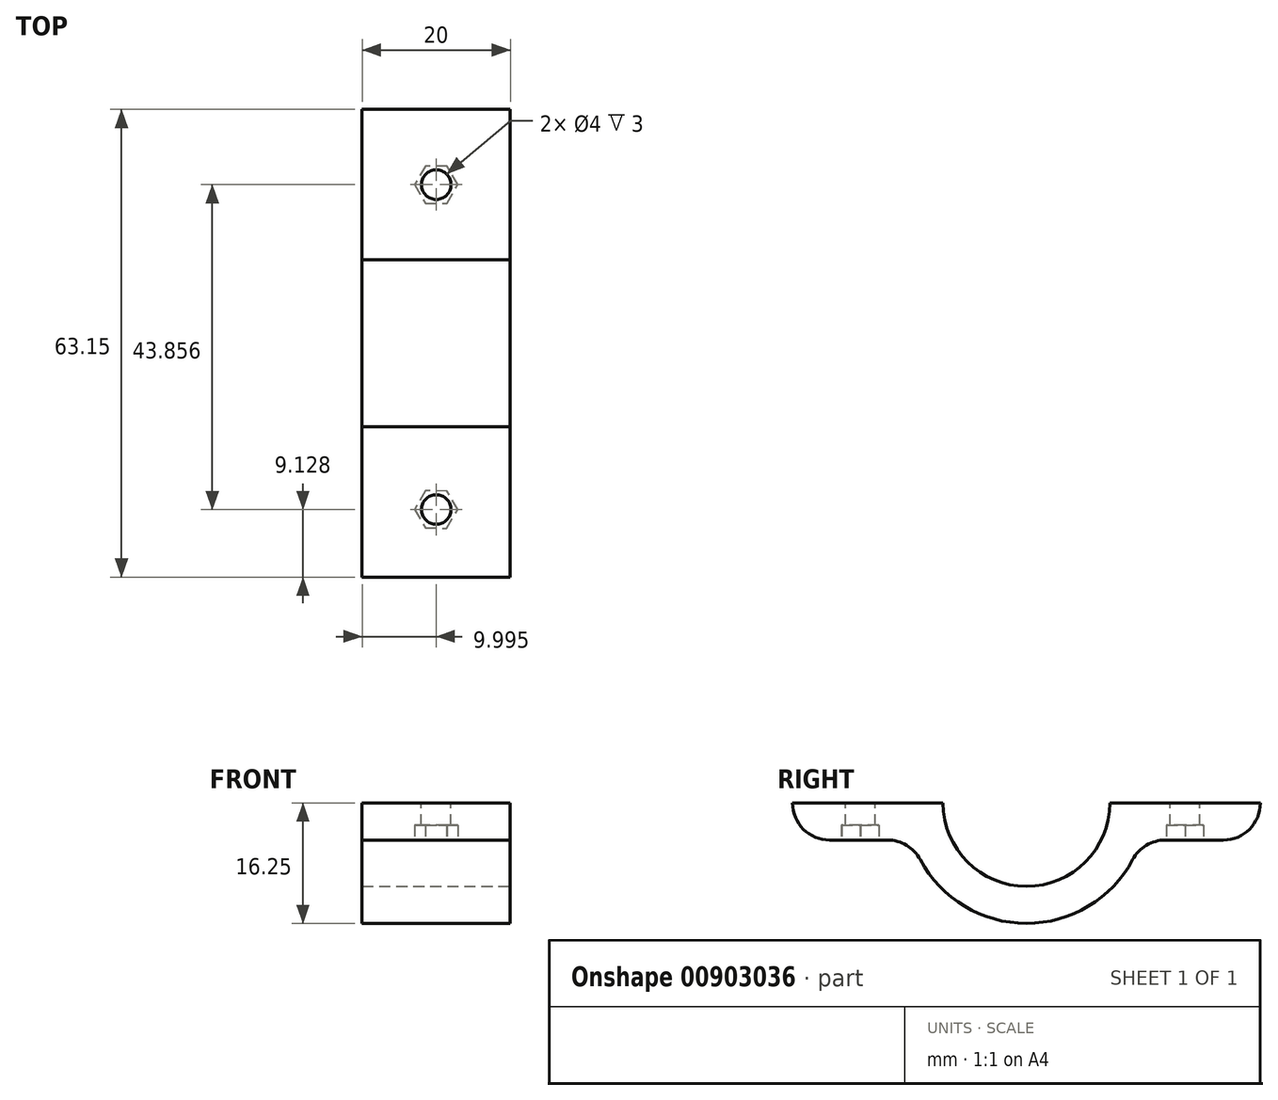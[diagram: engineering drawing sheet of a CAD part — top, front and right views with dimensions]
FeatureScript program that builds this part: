
annotation { "Feature Type Name" : "Feature", "Feature Type Description" : "" }
export const myFeature = defineFeature(function(context is Context, id is Id, definition is map)
    precondition{}
    {
        {
            var Q0;
            Q0=qCreatedBy(makeId("Top.planeOp"),FACE);
            var sketch = newSketch(context, id + "F0", { "sketchPlane" : qUnion([Q0])});
            skLineSegment(sketch, "E0.bottom", {"start": v(-81.43, 66.57) * mm, "end": v(-51.43, 66.57) * mm});
            skLineSegment(sketch, "E0.top", {"start": v(-81.43, -43.43) * mm, "end": v(-6.43, -43.43) * mm});
            skLineSegment(sketch, "E0.left", {"start": v(-81.43, 66.57) * mm, "end": v(-81.43, -43.43) * mm});
            skLineSegment(sketch, "E0.right", {"start": v(98.57, 66.57) * mm, "end": v(98.57, -43.43) * mm});
            skLineSegment(sketch, "E1", {"start": v(-81.43, 96.12) * mm, "end": v(8.57, 96.12) * mm, "construction": true});
            skPoint(sketch, "E1.endSnap0", {"position": v(8.57, 66.57) * mm});
            skLineSegment(sketch, "E2", {"start": v(8.57, 96.12) * mm, "end": v(98.57, 96.12) * mm, "construction": true});
            skLineSegment(sketch, "E3", {"start": v(-36.43, 81.57) * mm, "end": v(-36.43, 66.57) * mm, "construction": true});
            skLineSegment(sketch, "E4", {"start": v(53.57, 81.57) * mm, "end": v(53.57, 66.57) * mm, "construction": true});
            skArc(sketch, "E5", {"start": v(-21.43, 66.57) * mm, "mid": v(-36.43, 81.57) * mm, "end": v(-51.43, 66.57) * mm});
            skArc(sketch, "E6", {"start": v(68.57, 66.57) * mm, "mid": v(53.57, 81.57) * mm, "end": v(38.57, 66.57) * mm});
            skArc(sketch, "E7", {"start": v(-6.43, -43.43) * mm, "mid": v(8.57, -58.43) * mm, "end": v(23.57, -43.43) * mm});
            skLineSegment(sketch, "E8.trimOffspring", {"start": v(23.57, -43.43) * mm, "end": v(98.57, -43.43) * mm});
            skLineSegment(sketch, "E9.trimOffspring", {"start": v(-21.43, 66.57) * mm, "end": v(38.57, 66.57) * mm});
            skLineSegment(sketch, "E10.trimOffspring", {"start": v(68.57, 66.57) * mm, "end": v(98.57, 66.57) * mm});
            skPoint(sketch, "E11.orphan", {"position": v(53.57, 96.12) * mm});
            skPoint(sketch, "E12.orphan", {"position": v(-36.43, 96.12) * mm});
            skLineSegment(sketch, "E13", {"start": v(53.57, 74.07) * mm, "end": v(-36.43, 74.07) * mm, "construction": true});
            skLineSegment(sketch, "E14", {"start": v(8.57, -58.43) * mm, "end": v(8.57, -43.43) * mm, "construction": true});
            skCircle(sketch, "E15", {"center": v(8.57, -50.93) * mm, "radius": 2 * mm});
            skCircle(sketch, "E16", {"center": v(53.57, 74.07) * mm, "radius": 2 * mm});
            skCircle(sketch, "E17", {"center": v(-36.43, 74.07) * mm, "radius": 2 * mm});
            skSolve(sketch);
        }
        {
            var Q0;
            Q0=qSketchRegion(id+"F0",true);
            extrude(context, id + "F1", {"entities" : qUnion([Q0]), "depth" : 25 * mm, "offsetDistance" : 25 * mm});
        }
        {
            var Q0;
            Q0=makeQuery(id+"F1.opExtrude","SWEPT_FACE",FACE,{"disambiguationData":[OSD([sQuery(id+"F0.wireOp",EDGE,"E0.right")])]});
            var sketch = newSketch(context, id + "F2", { "sketchPlane" : qUnion([Q0])});
            skArc(sketch, "E18", {"start": v(22.82, 0) * mm, "mid": v(11.57, 11.25) * mm, "end": v(0.32, 0) * mm});
            skLineSegment(sketch, "E19", {"start": v(-64.9, 25) * mm, "end": v(-64.9, 15) * mm, "construction": true});
            skLineSegment(sketch, "E20", {"start": v(-64.9, 15) * mm, "end": v(92.3, 15) * mm, "construction": true});
            skArc(sketch, "E21", {"start": v(-20, 0) * mm, "mid": v(-41.23, 11.15) * mm, "end": v(-64.9, 15) * mm});
            skLineSegment(sketch, "E22", {"start": v(11.57, 0) * mm, "end": v(11.57, -67.92) * mm, "construction": true});
            skArc(sketch, "E23.MirrorCS", {"start": v(43.15, 0) * mm, "mid": v(64.38, 11.15) * mm, "end": v(88.05, 15) * mm});
            skLineSegment(sketch, "E24", {"start": v(88.05, 15) * mm, "end": v(88.05, -16.41) * mm});
            skLineSegment(sketch, "E25", {"start": v(88.05, -16.41) * mm, "end": v(-64.9, -16.41) * mm});
            skLineSegment(sketch, "E26", {"start": v(-64.9, -16.41) * mm, "end": v(-64.9, 15) * mm});
            skLineSegment(sketch, "E27", {"start": v(-20, 0) * mm, "end": v(0.32, 0) * mm});
            skLineSegment(sketch, "E28.MirrorCS", {"start": v(43.15, 0) * mm, "end": v(22.82, 0) * mm});
            skSolve(sketch);
        }
        {
            var Q0;
            Q0=qSketchRegion(id+"F2",true);
            extrude(context, id + "F3", {"entities" : qUnion([Q0]), "operationType" : NewBodyOperationType.REMOVE, "oppositeDirection" : true, "depth" : 276 * mm, "offsetDistance" : 25 * mm});
        }
        {
            var Q0;
            Q0=makeQuery(id+"F1.opExtrude","CAP_FACE",FACE,{"disambiguationData":[OSD([sQuery(id+"F0.wireOp",EDGE,"E0.bottom"),sQuery(id+"F0.wireOp",EDGE,"E0.top"),sQuery(id+"F0.wireOp",EDGE,"E0.left"),sQuery(id+"F0.wireOp",EDGE,"E0.right"),sQuery(id+"F0.wireOp",EDGE,"E5"),sQuery(id+"F0.wireOp",EDGE,"E6"),sQuery(id+"F0.wireOp",EDGE,"E7"),sQuery(id+"F0.wireOp",EDGE,"E8.trimOffspring"),sQuery(id+"F0.wireOp",EDGE,"E9.trimOffspring"),sQuery(id+"F0.wireOp",EDGE,"E10.trimOffspring"),sQuery(id+"F0.wireOp",EDGE,"E15"),sQuery(id+"F0.wireOp",EDGE,"E16"),sQuery(id+"F0.wireOp",EDGE,"E17")])],"isStart":false});
            var sketch = newSketch(context, id + "F4", { "sketchPlane" : qUnion([Q0])});
            skLineSegment(sketch, "E29", {"start": v(-66.43, 11.57) * mm, "end": v(83.57, 11.57) * mm, "construction": true});
            skPoint(sketch, "E30", {"position": v(63.57, 11.57) * mm});
            skPoint(sketch, "E31", {"position": v(-46.43, 11.57) * mm});
            skLineSegment(sketch, "E32", {"start": v(-66.43, 11.57) * mm, "end": v(-46.43, 11.57) * mm, "construction": true});
            skLineSegment(sketch, "E33", {"start": v(63.57, 11.57) * mm, "end": v(83.57, 11.57) * mm, "construction": true});
            skLineSegment(sketch, "E34", {"start": v(-56.43, 11.57) * mm, "end": v(-56.43, 22.87) * mm, "construction": true});
            skLineSegment(sketch, "E35", {"start": v(73.57, 11.57) * mm, "end": v(73.57, 22.87) * mm, "construction": true});
            skLineSegment(sketch, "E36", {"start": v(-56.43, 22.87) * mm, "end": v(-56.43, 42.87) * mm, "construction": true});
            skLineSegment(sketch, "E37", {"start": v(73.57, 22.87) * mm, "end": v(73.57, 42.87) * mm, "construction": true});
            skCircle(sketch, "E38", {"center": v(-56.43, 32.87) * mm, "radius": 2 * mm});
            skCircle(sketch, "E39", {"center": v(73.57, 32.87) * mm, "radius": 2 * mm});
            skLineSegment(sketch, "E40", {"start": v(-81.43, 11.57) * mm, "end": v(98.57, 11.57) * mm, "construction": true});
            skCircle(sketch, "E41.MirrorC", {"center": v(-56.43, -9.73) * mm, "radius": 2 * mm});
            skCircle(sketch, "E42.MirrorC", {"center": v(73.57, -9.73) * mm, "radius": 2 * mm});
            skPoint(sketch, "E43", {"position": v(8.57, 11.57) * mm});
            skSolve(sketch);
        }
        {
            var Q0;
            Q0=qSketchRegion(id+"F4",true);
            extrude(context, id + "F5", {"entities" : qUnion([Q0]), "operationType" : NewBodyOperationType.REMOVE, "oppositeDirection" : true, "depth" : 84.8 * mm, "offsetDistance" : 25 * mm});
        }
        {
            var Q0;
            Q0=makeQuery(id+"F1.opExtrude","CAP_FACE",FACE,{"disambiguationData":[OSD([sQuery(id+"F0.wireOp",EDGE,"E0.bottom"),sQuery(id+"F0.wireOp",EDGE,"E0.top"),sQuery(id+"F0.wireOp",EDGE,"E0.left"),sQuery(id+"F0.wireOp",EDGE,"E0.right"),sQuery(id+"F0.wireOp",EDGE,"E5"),sQuery(id+"F0.wireOp",EDGE,"E6"),sQuery(id+"F0.wireOp",EDGE,"E7"),sQuery(id+"F0.wireOp",EDGE,"E8.trimOffspring"),sQuery(id+"F0.wireOp",EDGE,"E9.trimOffspring"),sQuery(id+"F0.wireOp",EDGE,"E10.trimOffspring"),sQuery(id+"F0.wireOp",EDGE,"E15"),sQuery(id+"F0.wireOp",EDGE,"E16"),sQuery(id+"F0.wireOp",EDGE,"E17")])],"isStart":false});
            var sketch = newSketch(context, id + "F6", { "sketchPlane" : qUnion([Q0])});
            skCircle(sketch, "E44", {"center": v(-56.43, 32.87) * mm, "radius": 2.5 * mm});
            skCircle(sketch, "E45", {"center": v(73.57, 32.87) * mm, "radius": 2.5 * mm});
            skCircle(sketch, "E46", {"center": v(73.57, -9.73) * mm, "radius": 2.5 * mm});
            skCircle(sketch, "E47", {"center": v(-56.43, -9.73) * mm, "radius": 2.5 * mm});
            skSolve(sketch);
        }
        {
            var Q0;
            Q0=qSketchRegion(id+"F6",true);
            extrude(context, id + "F7", {"entities" : qUnion([Q0]), "operationType" : NewBodyOperationType.REMOVE, "oppositeDirection" : true, "depth" : 5 * mm, "offsetDistance" : 25 * mm});
        }
        {
            var Q0;
            Q0=makeQuery(id+"F1.opExtrude","SWEPT_FACE",FACE,{"disambiguationData":[OSD([sQuery(id+"F0.wireOp",EDGE,"E0.left")])]});
            var sketch = newSketch(context, id + "F8", { "sketchPlane" : qUnion([Q0])});
            skArc(sketch, "E48", {"start": v(-22.82, 0) * mm, "mid": v(-11.57, -11.25) * mm, "end": v(-0.32, 0) * mm});
            skLineSegment(sketch, "E49", {"start": v(-43.15, 0) * mm, "end": v(-43.15, 0) * mm});
            skLineSegment(sketch, "E50", {"start": v(20, 0) * mm, "end": v(20, 0) * mm});
            skArc(sketch, "E51", {"start": v(-25.91, -7.65) * mm, "mid": v(-11.57, -16.25) * mm, "end": v(2.77, -7.65) * mm});
            skLineSegment(sketch, "E52", {"start": v(15, -5) * mm, "end": v(7.18, -5) * mm});
            skLineSegment(sketch, "E53", {"start": v(-38.15, -5) * mm, "end": v(-30.32, -5) * mm});
            skLineSegment(sketch, "E54", {"start": v(-43.15, 0) * mm, "end": v(-22.82, 0) * mm});
            skLineSegment(sketch, "E55", {"start": v(-0.32, 0) * mm, "end": v(20, 0) * mm});
            skPoint(sketch, "E56.visualSharp", {"position": v(-43.15, -5) * mm});
            skArc(sketch, "E56.filletArc", {"start": v(-43.15, 0) * mm, "mid": v(-41.68, -3.54) * mm, "end": v(-38.15, -5) * mm});
            skPoint(sketch, "E57.visualSharp", {"position": v(20, -5) * mm});
            skArc(sketch, "E57.filletArc", {"start": v(15, -5) * mm, "mid": v(18.54, -3.54) * mm, "end": v(20, 0) * mm});
            skPoint(sketch, "E58.visualSharp", {"position": v(-27.03, -5) * mm});
            skArc(sketch, "E58.filletArc", {"start": v(-25.91, -7.65) * mm, "mid": v(-27.75, -5.71) * mm, "end": v(-30.32, -5) * mm});
            skPoint(sketch, "E59.visualSharp", {"position": v(3.89, -5) * mm});
            skArc(sketch, "E59.filletArc", {"start": v(7.18, -5) * mm, "mid": v(4.6, -5.71) * mm, "end": v(2.77, -7.65) * mm});
            skSolve(sketch);
        }
        {
            var Q0;
            Q0 = qSketchRegion(id + "F8", true);
            extrude(context, id + "F9", {"entities" : qUnion([Q0]), "depth" : 20 * mm, "offsetDistance" : 25 * mm});
        }
        {
            var Q0;
            Q0=makeQuery(id+"F9.opExtrude","SWEPT_FACE",FACE,{"disambiguationData":[OSD([sQuery(id+"F8.wireOp",EDGE,"E54")])]});
            var sketch = newSketch(context, id + "F10", { "sketchPlane" : qUnion([Q0])});
            skLineSegment(sketch, "E60", {"start": v(-91.43, 43.15) * mm, "end": v(-91.43, 22.82) * mm, "construction": true});
            skCircle(sketch, "E61", {"center": v(-91.43, 32.98) * mm, "radius": 2 * mm});
            skLineSegment(sketch, "E62", {"start": v(-101.2, 11.06) * mm, "end": v(-27.2, 11.06) * mm, "construction": true});
            skCircle(sketch, "E63.MirrorC", {"center": v(-91.43, -10.87) * mm, "radius": 2 * mm});
            skSolve(sketch);
        }
        {
            var Q0;
            Q0 = qSketchRegion(id + "F10", true);
            extrude(context, id + "F11", {"entities" : qUnion([Q0]), "operationType" : NewBodyOperationType.REMOVE, "oppositeDirection" : true, "depth" : 25 * mm, "offsetDistance" : 25 * mm});
        }
        {
            var Q0;
            Q0=makeQuery(id+"F9.opExtrude","SWEPT_FACE",FACE,{"disambiguationData":[OSD([sQuery(id+"F8.wireOp",EDGE,"E53")])]});
            var sketch = newSketch(context, id + "F12", { "sketchPlane" : qUnion([Q0])});
            skCircle(sketch, "E64.cCircle", {"center": v(-91.43, -32.98) * mm, "radius": 2.9 * mm, "construction": true});
            skLineSegment(sketch, "E64.0", {"start": v(-88.53, -32.98) * mm, "end": v(-89.98, -35.5) * mm});
            skLineSegment(sketch, "E64.1", {"start": v(-89.98, -35.5) * mm, "end": v(-92.88, -35.5) * mm});
            skLineSegment(sketch, "E64.2", {"start": v(-92.88, -35.5) * mm, "end": v(-94.33, -32.99) * mm});
            skLineSegment(sketch, "E64.3", {"start": v(-94.33, -32.99) * mm, "end": v(-92.89, -30.47) * mm});
            skLineSegment(sketch, "E64.4", {"start": v(-92.89, -30.47) * mm, "end": v(-89.99, -30.47) * mm});
            skLineSegment(sketch, "E64.5", {"start": v(-89.99, -30.47) * mm, "end": v(-88.53, -32.98) * mm});
            skSolve(sketch);
        }
        {
            var Q0;
            Q0=makeQuery(id+"F9.opExtrude","SWEPT_FACE",FACE,{"disambiguationData":[OSD([sQuery(id+"F8.wireOp",EDGE,"E52")])]});
            var sketch = newSketch(context, id + "F13", { "sketchPlane" : qUnion([Q0])});
            skCircle(sketch, "E65.cCircle", {"center": v(-91.43, 10.87) * mm, "radius": 2.9 * mm, "construction": true});
            skLineSegment(sketch, "E65.0", {"start": v(-88.53, 10.9) * mm, "end": v(-89.97, 8.37) * mm});
            skLineSegment(sketch, "E65.1", {"start": v(-89.97, 8.37) * mm, "end": v(-92.87, 8.35) * mm});
            skLineSegment(sketch, "E65.2", {"start": v(-92.87, 8.35) * mm, "end": v(-94.33, 10.85) * mm});
            skLineSegment(sketch, "E65.3", {"start": v(-94.33, 10.85) * mm, "end": v(-92.9, 13.37) * mm});
            skLineSegment(sketch, "E65.4", {"start": v(-92.9, 13.37) * mm, "end": v(-90, 13.4) * mm});
            skLineSegment(sketch, "E65.5", {"start": v(-90, 13.4) * mm, "end": v(-88.53, 10.9) * mm});
            skSolve(sketch);
        }
        {
            var Q0;
            Q0 = qSketchRegion(id + "F13", true);
            var Q1;
            Q1 = qSketchRegion(id + "F12", true);
            extrude(context, id + "F14", {"entities" : qUnion([Q0, Q1]), "operationType" : NewBodyOperationType.REMOVE, "oppositeDirection" : true, "depth" : 2 * mm, "offsetDistance" : 25 * mm});
        }
        {
            var Q0;
            Q0=makeQuery(id+"F1.opExtrude","SWEPT_BODY",BODY,{"disambiguationData":[OSD([sQuery(id+"F0.wireOp",EDGE,"E0.bottom"),sQuery(id+"F0.wireOp",EDGE,"E0.top"),sQuery(id+"F0.wireOp",EDGE,"E0.left"),sQuery(id+"F0.wireOp",EDGE,"E0.right"),sQuery(id+"F0.wireOp",EDGE,"E5"),sQuery(id+"F0.wireOp",EDGE,"E6"),sQuery(id+"F0.wireOp",EDGE,"E7"),sQuery(id+"F0.wireOp",EDGE,"E8.trimOffspring"),sQuery(id+"F0.wireOp",EDGE,"E9.trimOffspring"),sQuery(id+"F0.wireOp",EDGE,"E10.trimOffspring"),sQuery(id+"F0.wireOp",EDGE,"E15"),sQuery(id+"F0.wireOp",EDGE,"E16"),sQuery(id+"F0.wireOp",EDGE,"E17")])]});
            deleteBodies(context, id + "F15", {"entities" : qUnion([Q0])});
        }
    });
